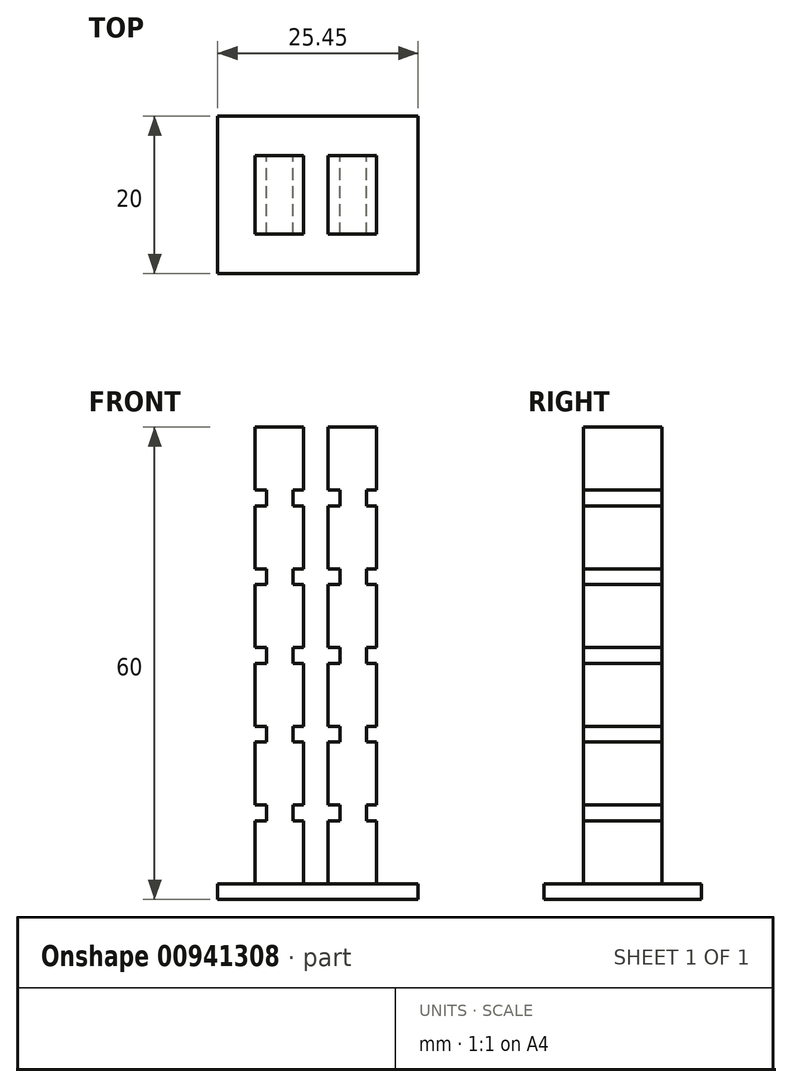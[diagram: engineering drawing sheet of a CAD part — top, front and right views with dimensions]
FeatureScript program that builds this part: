
annotation { "Feature Type Name" : "Feature", "Feature Type Description" : "" }
export const myFeature = defineFeature(function(context is Context, id is Id, definition is map)
    precondition{}
    {
        {
            var Q0;
            Q0=qCreatedBy(makeId("Front.planeOp"),FACE);
            var sketch = newSketch(context, id + "F0", { "sketchPlane" : qUnion([Q0])});
            skLineSegment(sketch, "E0.bottom", {"start": v(-69.82, 0) * mm, "end": v(-44.37, 0) * mm});
            skLineSegment(sketch, "E0.top", {"start": v(-69.82, 2) * mm, "end": v(-44.37, 2) * mm});
            skLineSegment(sketch, "E0.left", {"start": v(-69.82, 0) * mm, "end": v(-69.82, 2) * mm});
            skLineSegment(sketch, "E0.right", {"start": v(-44.37, 0) * mm, "end": v(-44.37, 2) * mm});
            skLineSegment(sketch, "E1.bottom", {"start": v(-65.1, 10) * mm, "end": v(-58.92, 10) * mm});
            skLineSegment(sketch, "E1.top", {"start": v(-65.1, 2) * mm, "end": v(-58.92, 2) * mm});
            skLineSegment(sketch, "E1.left", {"start": v(-65.1, 10) * mm, "end": v(-65.1, 2) * mm});
            skLineSegment(sketch, "E1.right", {"start": v(-58.92, 10) * mm, "end": v(-58.92, 2) * mm});
            skLineSegment(sketch, "E2.bottom", {"start": v(-63.6, 12) * mm, "end": v(-60.22, 12) * mm});
            skLineSegment(sketch, "E2.top", {"start": v(-63.6, 10) * mm, "end": v(-60.22, 10) * mm});
            skLineSegment(sketch, "E2.left", {"start": v(-63.6, 12) * mm, "end": v(-63.6, 10) * mm});
            skLineSegment(sketch, "E2.right", {"start": v(-60.22, 12) * mm, "end": v(-60.22, 10) * mm});
            skLineSegment(sketch, "E3.0.1.0", {"start": v(-65.1, 12) * mm, "end": v(-58.92, 12) * mm});
            skLineSegment(sketch, "E3.0.1.1", {"start": v(-65.1, 20) * mm, "end": v(-65.1, 12) * mm});
            skLineSegment(sketch, "E3.0.1.2", {"start": v(-58.92, 20) * mm, "end": v(-58.92, 12) * mm});
            skLineSegment(sketch, "E3.0.1.3", {"start": v(-63.6, 20) * mm, "end": v(-60.22, 20) * mm});
            skLineSegment(sketch, "E3.0.1.4", {"start": v(-65.1, 20) * mm, "end": v(-58.92, 20) * mm});
            skLineSegment(sketch, "E3.0.1.5", {"start": v(-63.6, 22) * mm, "end": v(-63.6, 20) * mm});
            skLineSegment(sketch, "E3.0.1.6", {"start": v(-60.22, 22) * mm, "end": v(-60.22, 20) * mm});
            skLineSegment(sketch, "E3.0.1.7", {"start": v(-63.6, 22) * mm, "end": v(-60.22, 22) * mm});
            skLineSegment(sketch, "E3.0.2.0", {"start": v(-65.1, 22) * mm, "end": v(-58.92, 22) * mm});
            skLineSegment(sketch, "E3.0.2.1", {"start": v(-65.1, 30) * mm, "end": v(-65.1, 22) * mm});
            skLineSegment(sketch, "E3.0.2.2", {"start": v(-58.92, 30) * mm, "end": v(-58.92, 22) * mm});
            skLineSegment(sketch, "E3.0.2.3", {"start": v(-63.6, 30) * mm, "end": v(-60.22, 30) * mm});
            skLineSegment(sketch, "E3.0.2.4", {"start": v(-65.1, 30) * mm, "end": v(-58.92, 30) * mm});
            skLineSegment(sketch, "E3.0.2.5", {"start": v(-63.6, 32) * mm, "end": v(-63.6, 30) * mm});
            skLineSegment(sketch, "E3.0.2.6", {"start": v(-60.22, 32) * mm, "end": v(-60.22, 30) * mm});
            skLineSegment(sketch, "E3.0.2.7", {"start": v(-63.6, 32) * mm, "end": v(-60.22, 32) * mm});
            skLineSegment(sketch, "E3.0.3.0", {"start": v(-65.1, 32) * mm, "end": v(-58.92, 32) * mm});
            skLineSegment(sketch, "E3.0.3.1", {"start": v(-65.1, 40) * mm, "end": v(-65.1, 32) * mm});
            skLineSegment(sketch, "E3.0.3.2", {"start": v(-58.92, 40) * mm, "end": v(-58.92, 32) * mm});
            skLineSegment(sketch, "E3.0.3.3", {"start": v(-63.6, 40) * mm, "end": v(-60.22, 40) * mm});
            skLineSegment(sketch, "E3.0.3.4", {"start": v(-65.1, 40) * mm, "end": v(-58.92, 40) * mm});
            skLineSegment(sketch, "E3.0.3.5", {"start": v(-63.6, 42) * mm, "end": v(-63.6, 40) * mm});
            skLineSegment(sketch, "E3.0.3.6", {"start": v(-60.22, 42) * mm, "end": v(-60.22, 40) * mm});
            skLineSegment(sketch, "E3.0.3.7", {"start": v(-63.6, 42) * mm, "end": v(-60.22, 42) * mm});
            skLineSegment(sketch, "E3.0.4.0", {"start": v(-65.1, 42) * mm, "end": v(-58.92, 42) * mm});
            skLineSegment(sketch, "E3.0.4.1", {"start": v(-65.1, 50) * mm, "end": v(-65.1, 42) * mm});
            skLineSegment(sketch, "E3.0.4.2", {"start": v(-58.92, 50) * mm, "end": v(-58.92, 42) * mm});
            skLineSegment(sketch, "E3.0.4.3", {"start": v(-63.6, 50) * mm, "end": v(-60.22, 50) * mm});
            skLineSegment(sketch, "E3.0.4.4", {"start": v(-65.1, 50) * mm, "end": v(-58.92, 50) * mm});
            skLineSegment(sketch, "E3.0.4.5", {"start": v(-63.6, 52) * mm, "end": v(-63.6, 50) * mm});
            skLineSegment(sketch, "E3.0.4.6", {"start": v(-60.22, 52) * mm, "end": v(-60.22, 50) * mm});
            skLineSegment(sketch, "E3.0.4.7", {"start": v(-63.6, 52) * mm, "end": v(-60.22, 52) * mm});
            skLineSegment(sketch, "E3.0.5.0", {"start": v(-65.1, 52) * mm, "end": v(-58.92, 52) * mm});
            skLineSegment(sketch, "E3.0.5.1", {"start": v(-65.1, 60) * mm, "end": v(-65.1, 52) * mm});
            skLineSegment(sketch, "E3.0.5.2", {"start": v(-58.92, 60) * mm, "end": v(-58.92, 52) * mm});
            skLineSegment(sketch, "E3.0.5.3", {"start": v(-63.6, 60) * mm, "end": v(-60.22, 60) * mm});
            skLineSegment(sketch, "E3.0.5.4", {"start": v(-65.1, 60) * mm, "end": v(-58.92, 60) * mm});
            skLineSegment(sketch, "E3.0.5.5", {"start": v(-63.6, 62) * mm, "end": v(-63.6, 60) * mm});
            skLineSegment(sketch, "E3.0.5.6", {"start": v(-60.22, 62) * mm, "end": v(-60.22, 60) * mm});
            skLineSegment(sketch, "E3.0.5.7", {"start": v(-63.6, 62) * mm, "end": v(-60.22, 62) * mm});
            skLineSegment(sketch, "E3.1.0.0", {"start": v(-55.8, 2) * mm, "end": v(-49.62, 2) * mm});
            skLineSegment(sketch, "E3.1.0.1", {"start": v(-55.8, 10) * mm, "end": v(-55.8, 2) * mm});
            skLineSegment(sketch, "E3.1.0.2", {"start": v(-49.62, 10) * mm, "end": v(-49.62, 2) * mm});
            skLineSegment(sketch, "E3.1.0.3", {"start": v(-54.3, 10) * mm, "end": v(-50.92, 10) * mm});
            skLineSegment(sketch, "E3.1.0.4", {"start": v(-55.8, 10) * mm, "end": v(-49.62, 10) * mm});
            skLineSegment(sketch, "E3.1.0.5", {"start": v(-54.3, 12) * mm, "end": v(-54.3, 10) * mm});
            skLineSegment(sketch, "E3.1.0.6", {"start": v(-50.92, 12) * mm, "end": v(-50.92, 10) * mm});
            skLineSegment(sketch, "E3.1.0.7", {"start": v(-54.3, 12) * mm, "end": v(-50.92, 12) * mm});
            skLineSegment(sketch, "E3.1.1.0", {"start": v(-55.8, 12) * mm, "end": v(-49.62, 12) * mm});
            skLineSegment(sketch, "E3.1.1.1", {"start": v(-55.8, 20) * mm, "end": v(-55.8, 12) * mm});
            skLineSegment(sketch, "E3.1.1.2", {"start": v(-49.62, 20) * mm, "end": v(-49.62, 12) * mm});
            skLineSegment(sketch, "E3.1.1.3", {"start": v(-54.3, 20) * mm, "end": v(-50.92, 20) * mm});
            skLineSegment(sketch, "E3.1.1.4", {"start": v(-55.8, 20) * mm, "end": v(-49.62, 20) * mm});
            skLineSegment(sketch, "E3.1.1.5", {"start": v(-54.3, 22) * mm, "end": v(-54.3, 20) * mm});
            skLineSegment(sketch, "E3.1.1.6", {"start": v(-50.92, 22) * mm, "end": v(-50.92, 20) * mm});
            skLineSegment(sketch, "E3.1.1.7", {"start": v(-54.3, 22) * mm, "end": v(-50.92, 22) * mm});
            skLineSegment(sketch, "E3.1.2.0", {"start": v(-55.8, 22) * mm, "end": v(-49.62, 22) * mm});
            skLineSegment(sketch, "E3.1.2.1", {"start": v(-55.8, 30) * mm, "end": v(-55.8, 22) * mm});
            skLineSegment(sketch, "E3.1.2.2", {"start": v(-49.62, 30) * mm, "end": v(-49.62, 22) * mm});
            skLineSegment(sketch, "E3.1.2.3", {"start": v(-54.3, 30) * mm, "end": v(-50.92, 30) * mm});
            skLineSegment(sketch, "E3.1.2.4", {"start": v(-55.8, 30) * mm, "end": v(-49.62, 30) * mm});
            skLineSegment(sketch, "E3.1.2.5", {"start": v(-54.3, 32) * mm, "end": v(-54.3, 30) * mm});
            skLineSegment(sketch, "E3.1.2.6", {"start": v(-50.92, 32) * mm, "end": v(-50.92, 30) * mm});
            skLineSegment(sketch, "E3.1.2.7", {"start": v(-54.3, 32) * mm, "end": v(-50.92, 32) * mm});
            skLineSegment(sketch, "E3.1.3.0", {"start": v(-55.8, 32) * mm, "end": v(-49.62, 32) * mm});
            skLineSegment(sketch, "E3.1.3.1", {"start": v(-55.8, 40) * mm, "end": v(-55.8, 32) * mm});
            skLineSegment(sketch, "E3.1.3.2", {"start": v(-49.62, 40) * mm, "end": v(-49.62, 32) * mm});
            skLineSegment(sketch, "E3.1.3.3", {"start": v(-54.3, 40) * mm, "end": v(-50.92, 40) * mm});
            skLineSegment(sketch, "E3.1.3.4", {"start": v(-55.8, 40) * mm, "end": v(-49.62, 40) * mm});
            skLineSegment(sketch, "E3.1.3.5", {"start": v(-54.3, 42) * mm, "end": v(-54.3, 40) * mm});
            skLineSegment(sketch, "E3.1.3.6", {"start": v(-50.92, 42) * mm, "end": v(-50.92, 40) * mm});
            skLineSegment(sketch, "E3.1.3.7", {"start": v(-54.3, 42) * mm, "end": v(-50.92, 42) * mm});
            skLineSegment(sketch, "E3.1.4.0", {"start": v(-55.8, 42) * mm, "end": v(-49.62, 42) * mm});
            skLineSegment(sketch, "E3.1.4.1", {"start": v(-55.8, 50) * mm, "end": v(-55.8, 42) * mm});
            skLineSegment(sketch, "E3.1.4.2", {"start": v(-49.62, 50) * mm, "end": v(-49.62, 42) * mm});
            skLineSegment(sketch, "E3.1.4.3", {"start": v(-54.3, 50) * mm, "end": v(-50.92, 50) * mm});
            skLineSegment(sketch, "E3.1.4.4", {"start": v(-55.8, 50) * mm, "end": v(-49.62, 50) * mm});
            skLineSegment(sketch, "E3.1.4.5", {"start": v(-54.3, 52) * mm, "end": v(-54.3, 50) * mm});
            skLineSegment(sketch, "E3.1.4.6", {"start": v(-50.92, 52) * mm, "end": v(-50.92, 50) * mm});
            skLineSegment(sketch, "E3.1.4.7", {"start": v(-54.3, 52) * mm, "end": v(-50.92, 52) * mm});
            skLineSegment(sketch, "E3.1.5.0", {"start": v(-55.8, 52) * mm, "end": v(-49.62, 52) * mm});
            skLineSegment(sketch, "E3.1.5.1", {"start": v(-55.8, 60) * mm, "end": v(-55.8, 52) * mm});
            skLineSegment(sketch, "E3.1.5.2", {"start": v(-49.62, 60) * mm, "end": v(-49.62, 52) * mm});
            skLineSegment(sketch, "E3.1.5.3", {"start": v(-54.3, 60) * mm, "end": v(-50.92, 60) * mm});
            skLineSegment(sketch, "E3.1.5.4", {"start": v(-55.8, 60) * mm, "end": v(-49.62, 60) * mm});
            skLineSegment(sketch, "E3.1.5.5", {"start": v(-54.3, 62) * mm, "end": v(-54.3, 60) * mm});
            skLineSegment(sketch, "E3.1.5.6", {"start": v(-50.92, 62) * mm, "end": v(-50.92, 60) * mm});
            skLineSegment(sketch, "E3.1.5.7", {"start": v(-54.3, 62) * mm, "end": v(-50.92, 62) * mm});
            skLineSegment(sketch, "E3.direction1", {"start": v(-65.1, 2) * mm, "end": v(-55.8, 2) * mm, "construction": true});
            skLineSegment(sketch, "E3.direction2", {"start": v(-65.1, 2) * mm, "end": v(-65.1, 12) * mm, "construction": true});
            skSolve(sketch);
        }
        {
            var Q0;
            Q0=makeQuery(id+"F0.imprint","IMPRINT",FACE,{"disambiguationData":[TD([[makeQuery(id+"F0.imprint","IMPRINT",EDGE,{"derivedFrom":sQuery(id+"F0.wireOp",EDGE,"E0.bottom")}),1.0]])]});
            extrude(context, id + "F1", {"entities" : qUnion([Q0]), "endBound" : BoundingType.SYMMETRIC, "depth" : 20 * mm, "offsetDistance" : 25 * mm});
        }
        {
            var Q0;
            {var subQ1=sQuery(id+"F0.wireOp",EDGE,"E3.1.0.1");Q0=makeQuery(id+"F0.imprint","IMPRINT",FACE,{"disambiguationData":[TD([[makeQuery(id+"F0.imprint","IMPRINT",EDGE,{"derivedFrom":subQ1}),1.0]])]});}
            var Q1;
            {var subQ4=sQuery(id+"F0.wireOp",EDGE,"E1.left");Q1=makeQuery(id+"F0.imprint","IMPRINT",FACE,{"disambiguationData":[TD([[makeQuery(id+"F0.imprint","IMPRINT",EDGE,{"derivedFrom":subQ4}),1.0]])]});}
            var Q2;
            {var subQ2=sQuery(id+"F0.wireOp",EDGE,"E3.0.1.7");Q2=makeQuery(id+"F0.imprint","IMPRINT",FACE,{"disambiguationData":[TD([[makeQuery(id+"F0.imprint","IMPRINT",EDGE,{"derivedFrom":subQ2}),1.0]])]});}
            var Q3;
            {var subQ2=sQuery(id+"F0.wireOp",EDGE,"E3.0.2.7");Q3=makeQuery(id+"F0.imprint","IMPRINT",FACE,{"disambiguationData":[TD([[makeQuery(id+"F0.imprint","IMPRINT",EDGE,{"derivedFrom":subQ2}),1.0]])]});}
            var Q4;
            Q4=makeQuery(id+"F0.imprint","IMPRINT",FACE,{"disambiguationData":[TD([[makeQuery(id+"F0.imprint","IMPRINT",EDGE,{"derivedFrom":sQuery(id+"F0.wireOp",EDGE,"E3.0.2.3")}),1.0]])]});
            var Q5;
            Q5=makeQuery(id+"F0.imprint","IMPRINT",FACE,{"disambiguationData":[TD([[makeQuery(id+"F0.imprint","IMPRINT",EDGE,{"derivedFrom":sQuery(id+"F0.wireOp",EDGE,"E3.1.4.3")}),1.0]])]});
            var Q6;
            Q6=makeQuery(id+"F0.imprint","IMPRINT",FACE,{"disambiguationData":[TD([[makeQuery(id+"F0.imprint","IMPRINT",EDGE,{"derivedFrom":sQuery(id+"F0.wireOp",EDGE,"E3.0.1.3")}),1.0]])]});
            var Q7;
            Q7=makeQuery(id+"F0.imprint","IMPRINT",FACE,{"disambiguationData":[TD([[makeQuery(id+"F0.imprint","IMPRINT",EDGE,{"derivedFrom":sQuery(id+"F0.wireOp",EDGE,"E3.1.0.3")}),1.0]])]});
            var Q8;
            {var subQ2=sQuery(id+"F0.wireOp",EDGE,"E3.1.3.7");Q8=makeQuery(id+"F0.imprint","IMPRINT",FACE,{"disambiguationData":[TD([[makeQuery(id+"F0.imprint","IMPRINT",EDGE,{"derivedFrom":subQ2}),1.0]])]});}
            var Q9;
            {var subQ2=sQuery(id+"F0.wireOp",EDGE,"E3.0.3.7");Q9=makeQuery(id+"F0.imprint","IMPRINT",FACE,{"disambiguationData":[TD([[makeQuery(id+"F0.imprint","IMPRINT",EDGE,{"derivedFrom":subQ2}),1.0]])]});}
            var Q10;
            Q10=makeQuery(id+"F0.imprint","IMPRINT",FACE,{"disambiguationData":[TD([[makeQuery(id+"F0.imprint","IMPRINT",EDGE,{"derivedFrom":sQuery(id+"F0.wireOp",EDGE,"E2.bottom")}),-1.0]])]});
            var Q11;
            Q11=makeQuery(id+"F0.imprint","IMPRINT",FACE,{"disambiguationData":[TD([[makeQuery(id+"F0.imprint","IMPRINT",EDGE,{"derivedFrom":sQuery(id+"F0.wireOp",EDGE,"E3.1.3.3")}),1.0]])]});
            var Q12;
            {var subQ2=sQuery(id+"F0.wireOp",EDGE,"E3.1.2.7");Q12=makeQuery(id+"F0.imprint","IMPRINT",FACE,{"disambiguationData":[TD([[makeQuery(id+"F0.imprint","IMPRINT",EDGE,{"derivedFrom":subQ2}),1.0]])]});}
            var Q13;
            {var subQ2=sQuery(id+"F0.wireOp",EDGE,"E3.1.0.7");Q13=makeQuery(id+"F0.imprint","IMPRINT",FACE,{"disambiguationData":[TD([[makeQuery(id+"F0.imprint","IMPRINT",EDGE,{"derivedFrom":subQ2}),1.0]])]});}
            var Q14;
            {var subQ2=sQuery(id+"F0.wireOp",EDGE,"E3.1.1.7");Q14=makeQuery(id+"F0.imprint","IMPRINT",FACE,{"disambiguationData":[TD([[makeQuery(id+"F0.imprint","IMPRINT",EDGE,{"derivedFrom":subQ2}),1.0]])]});}
            var Q15;
            Q15=makeQuery(id+"F0.imprint","IMPRINT",FACE,{"disambiguationData":[TD([[makeQuery(id+"F0.imprint","IMPRINT",EDGE,{"derivedFrom":sQuery(id+"F0.wireOp",EDGE,"E3.1.2.3")}),1.0]])]});
            var Q16;
            {var subQ1=sQuery(id+"F0.wireOp",EDGE,"E2.bottom");Q16=makeQuery(id+"F0.imprint","IMPRINT",FACE,{"disambiguationData":[TD([[makeQuery(id+"F0.imprint","IMPRINT",EDGE,{"derivedFrom":subQ1}),1.0]])]});}
            var Q17;
            {var subQ2=sQuery(id+"F0.wireOp",EDGE,"E3.1.4.7");Q17=makeQuery(id+"F0.imprint","IMPRINT",FACE,{"disambiguationData":[TD([[makeQuery(id+"F0.imprint","IMPRINT",EDGE,{"derivedFrom":subQ2}),1.0]])]});}
            var Q18;
            Q18=makeQuery(id+"F0.imprint","IMPRINT",FACE,{"disambiguationData":[TD([[makeQuery(id+"F0.imprint","IMPRINT",EDGE,{"derivedFrom":sQuery(id+"F0.wireOp",EDGE,"E3.0.4.3")}),1.0]])]});
            var Q19;
            Q19=makeQuery(id+"F0.imprint","IMPRINT",FACE,{"disambiguationData":[TD([[makeQuery(id+"F0.imprint","IMPRINT",EDGE,{"derivedFrom":sQuery(id+"F0.wireOp",EDGE,"E3.0.3.3")}),1.0]])]});
            var Q20;
            Q20=makeQuery(id+"F0.imprint","IMPRINT",FACE,{"disambiguationData":[TD([[makeQuery(id+"F0.imprint","IMPRINT",EDGE,{"derivedFrom":sQuery(id+"F0.wireOp",EDGE,"E3.1.1.3")}),1.0]])]});
            var Q21;
            {var subQ2=sQuery(id+"F0.wireOp",EDGE,"E3.0.4.7");Q21=makeQuery(id+"F0.imprint","IMPRINT",FACE,{"disambiguationData":[TD([[makeQuery(id+"F0.imprint","IMPRINT",EDGE,{"derivedFrom":subQ2}),1.0]])]});}
            extrude(context, id + "F2", {"entities" : qUnion([Q0, Q1, Q2, Q3, Q4, Q5, Q6, Q7, Q8, Q9, Q10, Q11, Q12, Q13, Q14, Q15, Q16, Q17, Q18, Q19, Q20, Q21]), "operationType" : NewBodyOperationType.ADD, "endBound" : BoundingType.SYMMETRIC, "depth" : 10 * mm, "offsetDistance" : 25 * mm});
        }
    });
